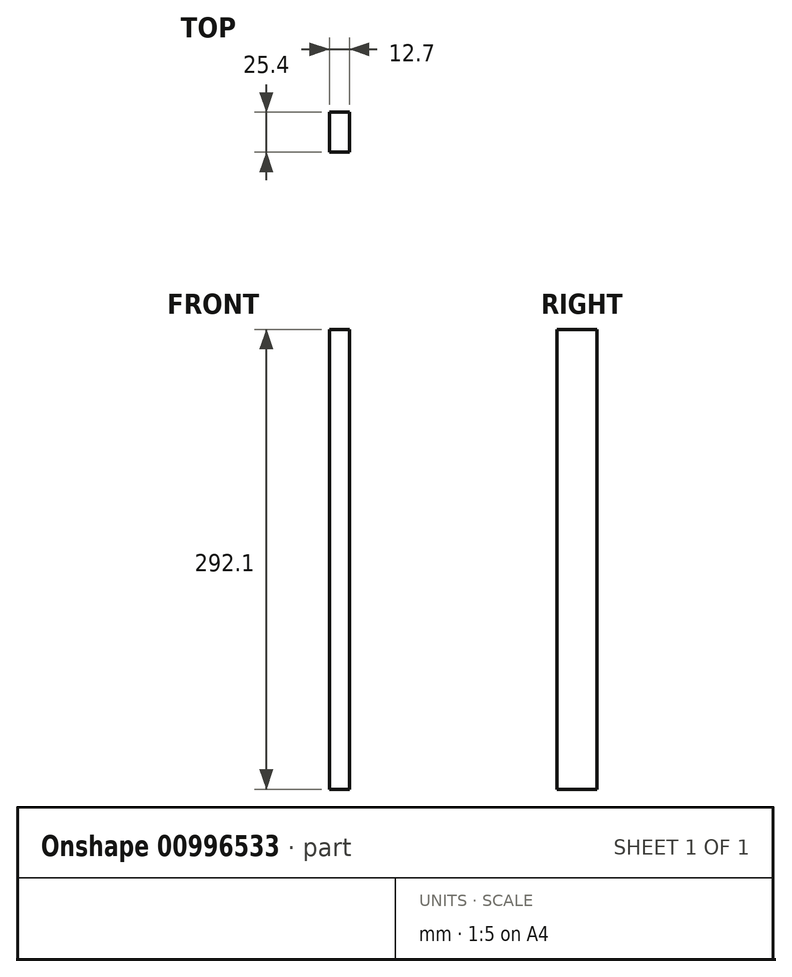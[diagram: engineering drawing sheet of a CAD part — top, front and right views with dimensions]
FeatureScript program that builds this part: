
annotation { "Feature Type Name" : "Feature", "Feature Type Description" : "" }
export const myFeature = defineFeature(function(context is Context, id is Id, definition is map)
    precondition{}
    {
        {
            var Q0;
            Q0=qCreatedBy(makeId("Right.planeOp"),FACE);
            var sketch = newSketch(context, id + "F0", { "sketchPlane" : qUnion([Q0])});
            skLineSegment(sketch, "E0.bottom", {"start": v(12.7, 146.05) * mm, "end": v(-12.7, 146.05) * mm});
            skLineSegment(sketch, "E0.top", {"start": v(12.7, -146.05) * mm, "end": v(-12.7, -146.05) * mm});
            skLineSegment(sketch, "E0.left", {"start": v(12.7, 146.05) * mm, "end": v(12.7, -146.05) * mm});
            skLineSegment(sketch, "E0.right", {"start": v(-12.7, 146.05) * mm, "end": v(-12.7, -146.05) * mm});
            skPoint(sketch, "E0.middle", {"position": v(0, 0) * mm});
            skSolve(sketch);
        }
        {
            var Q0;
            Q0=makeQuery(id+"F0.imprint","IMPRINT",FACE,{"disambiguationData":[TD([[makeQuery(id+"F0.imprint","IMPRINT",EDGE,{"derivedFrom":sQuery(id+"F0.wireOp",EDGE,"E0.bottom")}),1.0]])]});
            extrude(context, id + "F1", {"entities" : qUnion([Q0]), "depth" : 12.7 * mm, "offsetDistance" : 25.4 * mm});
        }
    });
